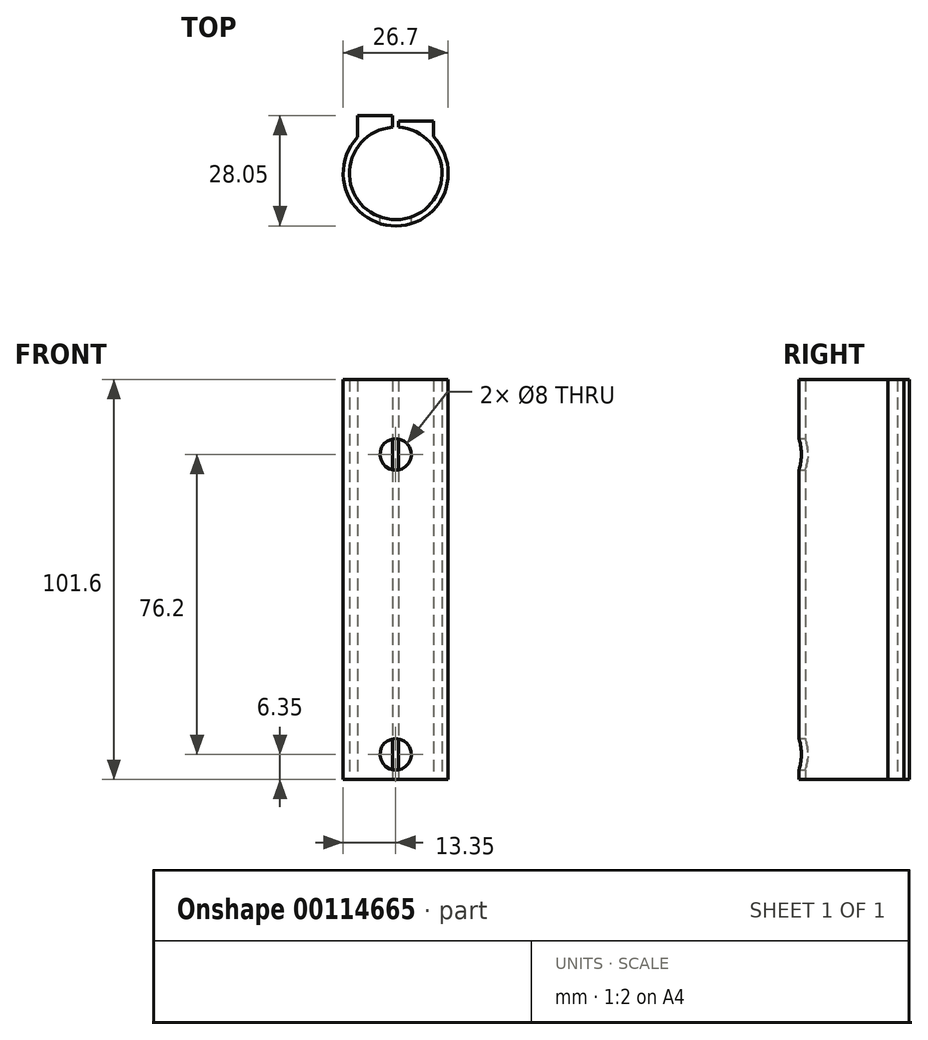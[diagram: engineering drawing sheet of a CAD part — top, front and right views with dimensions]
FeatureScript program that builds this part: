
annotation { "Feature Type Name" : "Feature", "Feature Type Description" : "" }
export const myFeature = defineFeature(function(context is Context, id is Id, definition is map)
    precondition{}
    {
        {
            var Q0;
            Q0=qCreatedBy(makeId("Top.planeOp"),FACE);
            var sketch = newSketch(context, id + "F0", { "sketchPlane" : qUnion([Q0])});
            skCircle(sketch, "E0", {"center": v(0, 0) * mm, "radius": 11.75 * mm});
            skLineSegment(sketch, "E1.bottom", {"start": v(-9.7, 6.64) * mm, "end": v(9.56, 6.64) * mm});
            skLineSegment(sketch, "E1.top", {"start": v(-9.7, 14.7) * mm, "end": v(9.56, 14.7) * mm});
            skLineSegment(sketch, "E1.left", {"start": v(-9.7, 6.64) * mm, "end": v(-9.7, 14.7) * mm});
            skLineSegment(sketch, "E1.right", {"start": v(9.56, 6.64) * mm, "end": v(9.56, 14.7) * mm});
            skCircle(sketch, "E2.0", {"center": v(0, 0) * mm, "radius": 13.35 * mm});
            skLineSegment(sketch, "E3.bottom", {"start": v(9.56, 14.7) * mm, "end": v(0, 14.7) * mm});
            skLineSegment(sketch, "E3.top", {"start": v(9.56, 13.35) * mm, "end": v(0, 13.35) * mm});
            skLineSegment(sketch, "E3.left", {"start": v(9.56, 14.7) * mm, "end": v(9.56, 13.35) * mm});
            skLineSegment(sketch, "E3.right", {"start": v(0, 14.7) * mm, "end": v(0, 13.35) * mm});
            skLineSegment(sketch, "E4.bottom", {"start": v(0, 13.35) * mm, "end": v(-9.7, 13.35) * mm});
            skLineSegment(sketch, "E4.top", {"start": v(0, 13.35) * mm, "end": v(-9.7, 13.35) * mm});
            skLineSegment(sketch, "E4.left", {"start": v(0, 13.35) * mm, "end": v(0, 13.35) * mm});
            skLineSegment(sketch, "E4.right", {"start": v(-9.7, 13.35) * mm, "end": v(-9.7, 13.35) * mm});
            skLineSegment(sketch, "E5.bottom", {"start": v(-0.87, 19.6) * mm, "end": v(0.73, 19.6) * mm});
            skLineSegment(sketch, "E5.top", {"start": v(-0.87, 6.88) * mm, "end": v(0.73, 6.88) * mm});
            skLineSegment(sketch, "E5.left", {"start": v(-0.87, 19.6) * mm, "end": v(-0.87, 6.88) * mm});
            skLineSegment(sketch, "E5.right", {"start": v(0.73, 19.6) * mm, "end": v(0.73, 6.88) * mm});
            skSolve(sketch);
        }
        {
            var Q0;
            {var subQ0=sQuery(id+"F0.wireOp",EDGE,"E3.left");Q0=makeQuery(id+"F0.imprint","IMPRINT",FACE,{"disambiguationData":[TD([[makeQuery(id+"F0.imprint","IMPRINT",EDGE,{"derivedFrom":subQ0}),-1.0]])]});}
            var Q1;
            {var subQ0=sQuery(id+"F0.wireOp",EDGE,"E1.left");var subQ1=sQuery(id+"F0.wireOp",EDGE,"E1.top");var subQ2=makeQuery(id+"F0.imprint","INTERSECT",VERTEX,{"derivedFrom":[subQ1,subQ0]});Q1=makeQuery(id+"F0.imprint","IMPRINT",FACE,{"disambiguationData":[TD([[makeQuery(id+"F0.imprint","IMPRINT",EDGE,{"disambiguationData":[TD([[subQ2,-1.0]])],"derivedFrom":subQ1}),-1.0]])]});}
            var Q2;
            {var subQ0=sQuery(id+"F0.wireOp",EDGE,"E4.top");var subQ1=sQuery(id+"F0.wireOp",EDGE,"E1.left");var subQ2=makeQuery(id+"F0.imprint","INTERSECT",VERTEX,{"derivedFrom":[subQ1,subQ0]});Q2=makeQuery(id+"F0.imprint","IMPRINT",FACE,{"disambiguationData":[TD([[makeQuery(id+"F0.imprint","IMPRINT",EDGE,{"disambiguationData":[TD([[subQ2,1.0]])],"derivedFrom":subQ1}),-1.0]])]});}
            var Q3;
            {var subQ0=sQuery(id+"F0.wireOp",EDGE,"E1.left");var subQ5=sQuery(id+"F0.wireOp",EDGE,"E2.0");var subQ6=makeQuery(id+"F0.imprint","INTERSECT",VERTEX,{"derivedFrom":[subQ0,subQ5]});Q3=makeQuery(id+"F0.imprint","IMPRINT",FACE,{"disambiguationData":[TD([[makeQuery(id+"F0.imprint","IMPRINT",EDGE,{"disambiguationData":[TD([[subQ6,1.0]])],"derivedFrom":subQ5}),1.0]])]});}
            var Q4;
            {var subQ1=sQuery(id+"F0.wireOp",EDGE,"E1.right");var subQ3=sQuery(id+"F0.wireOp",EDGE,"E2.0");var subQ4=makeQuery(id+"F0.imprint","INTERSECT",VERTEX,{"derivedFrom":[subQ1,subQ3]});Q4=makeQuery(id+"F0.imprint","IMPRINT",FACE,{"disambiguationData":[TD([[makeQuery(id+"F0.imprint","IMPRINT",EDGE,{"disambiguationData":[TD([[subQ4,-1.0]])],"derivedFrom":subQ3}),-1.0]])]});}
            var Q5;
            {var subQ0=sQuery(id+"F0.wireOp",EDGE,"E5.right");var subQ1=sQuery(id+"F0.wireOp",EDGE,"E0");var subQ2=makeQuery(id+"F0.imprint","INTERSECT",VERTEX,{"derivedFrom":[subQ1,subQ0]});Q5=makeQuery(id+"F0.imprint","IMPRINT",FACE,{"disambiguationData":[TD([[makeQuery(id+"F0.imprint","IMPRINT",EDGE,{"disambiguationData":[TD([[subQ2,1.0]])],"derivedFrom":subQ1}),-1.0]])]});}
            var Q6;
            {var subQ3=sQuery(id+"F0.wireOp",EDGE,"E1.right");var subQ5=sQuery(id+"F0.wireOp",EDGE,"E2.0");var subQ7=makeQuery(id+"F0.imprint","INTERSECT",VERTEX,{"derivedFrom":[subQ3,subQ5]});Q6=makeQuery(id+"F0.imprint","IMPRINT",FACE,{"disambiguationData":[TD([[makeQuery(id+"F0.imprint","IMPRINT",EDGE,{"disambiguationData":[TD([[subQ7,1.0]])],"derivedFrom":subQ3}),-1.0]])]});}
            extrude(context, id + "F1", {"entities" : qUnion([Q0, Q1, Q2, Q3, Q4, Q5, Q6]), "depth" : 101.6 * mm});
        }
        {
            var Q0;
            Q0=qCreatedBy(makeId("Front.planeOp"),FACE);
            var sketch = newSketch(context, id + "F2", { "sketchPlane" : qUnion([Q0])});
            skLineSegment(sketch, "E6", {"start": v(0, 0) * mm, "end": v(0, 6.35) * mm, "construction": true});
            skCircle(sketch, "E7", {"center": v(0, 6.35) * mm, "radius": 4 * mm});
            skLineSegment(sketch, "E8", {"start": v(0, 6.35) * mm, "end": v(0, 82.55) * mm});
            skCircle(sketch, "E9", {"center": v(0, 82.55) * mm, "radius": 4 * mm});
            skSolve(sketch);
        }
        {
            var Q0;
            Q0=makeQuery(id+"F2.imprint","IMPRINT",FACE,{"disambiguationData":[TD([[makeQuery(id+"F2.imprint","IMPRINT",EDGE,{"derivedFrom":sQuery(id+"F2.wireOp",EDGE,"E9")}),1.0]])]});
            var Q1;
            Q1=makeQuery(id+"F2.imprint","IMPRINT",FACE,{"disambiguationData":[TD([[makeQuery(id+"F2.imprint","IMPRINT",EDGE,{"derivedFrom":sQuery(id+"F2.wireOp",EDGE,"E7")}),1.0]])]});
            extrude(context, id + "F3", {"entities" : qUnion([Q0, Q1]), "depth" : 25.4 * mm});
        }
        {
            var Q0;
            Q0=makeQuery(id+"F3.opExtrude","SWEPT_BODY",BODY,{"disambiguationData":[OSD([sQuery(id+"F2.wireOp",EDGE,"E9")])]});
            var Q1;
            Q1=makeQuery(id+"F3.opExtrude","SWEPT_BODY",BODY,{"disambiguationData":[OSD([sQuery(id+"F2.wireOp",EDGE,"E7")])]});
            var Q2;
            Q2=makeQuery(id+"F1.opExtrude","SWEPT_BODY",BODY,{"disambiguationData":[OSD([sQuery(id+"F0.wireOp",EDGE,"E0"),sQuery(id+"F0.wireOp",EDGE,"E1.top"),sQuery(id+"F0.wireOp",EDGE,"E1.left"),sQuery(id+"F0.wireOp",EDGE,"E1.right"),sQuery(id+"F0.wireOp",EDGE,"E2.0"),sQuery(id+"F0.wireOp",EDGE,"E3.bottom"),sQuery(id+"F0.wireOp",EDGE,"E3.left"),sQuery(id+"F0.wireOp",EDGE,"E5.left"),sQuery(id+"F0.wireOp",EDGE,"E5.right")])]});
            booleanBodies(context, id + "F4", {"operationType" : BooleanOperationType.SUBTRACTION, "tools" : qUnion([Q0, Q1]), "targets" : qUnion([Q2])});
        }
    });
